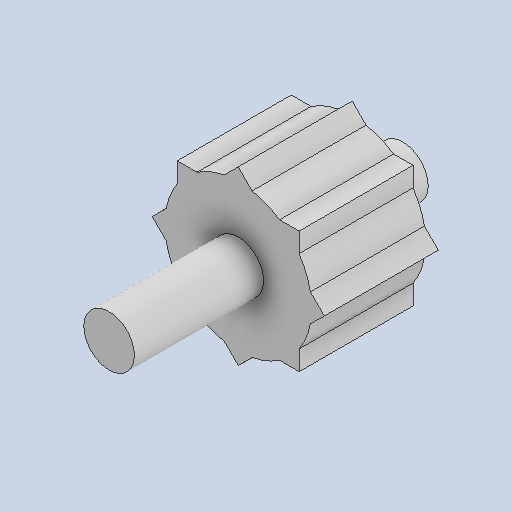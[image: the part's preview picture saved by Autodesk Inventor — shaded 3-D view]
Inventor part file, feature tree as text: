
AUTODESK INVENTOR PART (.ipt)
format: ipt  version: 2022.3 (Build 263350000, 350)  size: 158,720 bytes
history: native  units: mm
features: extrude x3, sketch x3, other x3, reference x2
ambient origin geometry x8: Origin, YZ Plane, XZ Plane, XY Plane, X Axis, Y Axis, Z Axis, Center Point
bodies: Solid1 (feature_tree)
feature tree (11):
  extrude  "Extrusion1"  Depth=5.1mm TaperAngle=0.0deg
  extrude  "Extrusion2"  Depth=2.0mm
  extrude  "Extrusion3"  Depth=2.0mm TaperAngle=360.0deg
  sketch  "Sketch1"  dims[d0=2.0mm d1=5.1mm d2=0.0mm]
  reference  "Reference1"
  sketch  "Sketch2"  dims[d3=1.2mm d4=2.0mm]
  reference  "Reference2"
  sketch  "Sketch3"  dims[d5=0.5mm d6=80.0mm d8=360.0deg d10=4.5mm d11=0.0mm d12=2.0mm d13=0.0mm]
  other  "<userpath>\Documents\Inventor\NanoSumo\NanoSumo_part1.iam"
  other  "NanoSumo_part1.iam"
  other  "bok:1"
